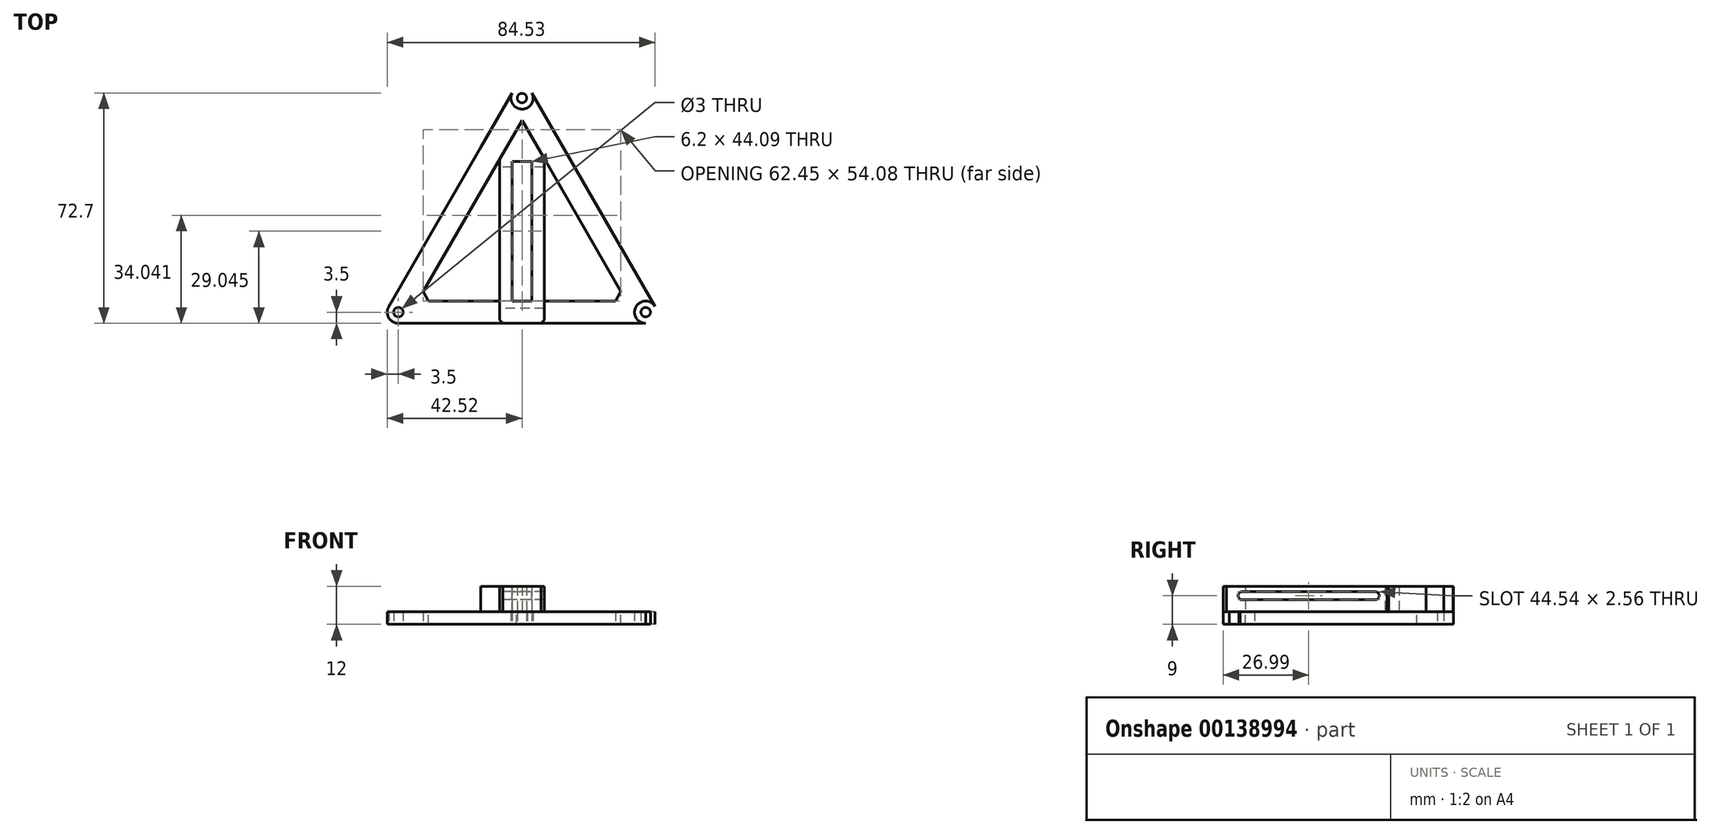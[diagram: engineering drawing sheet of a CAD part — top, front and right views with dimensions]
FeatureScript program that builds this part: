
annotation { "Feature Type Name" : "Feature", "Feature Type Description" : "" }
export const myFeature = defineFeature(function(context is Context, id is Id, definition is map)
    precondition{}
    {
        {
            var Q0;
            Q0=qCreatedBy(makeId("Top.planeOp"),FACE);
            var sketch = newSketch(context, id + "F0", { "sketchPlane" : qUnion([Q0])});
            skLineSegment(sketch, "E0", {"start": v(-21.7, -12.53) * mm, "end": v(0, 0) * mm});
            skLineSegment(sketch, "E1", {"start": v(-21.7, -12.53) * mm, "end": v(-39.02, -22.53) * mm, "construction": true});
            skCircle(sketch, "E2", {"center": v(-39.02, -22.53) * mm, "radius": 1.5 * mm});
            skLineSegment(sketch, "E3", {"start": v(-21.7, -12.53) * mm, "end": v(21.7, -12.53) * mm, "construction": true});
            skLineSegment(sketch, "E4", {"start": v(0, 25.06) * mm, "end": v(-21.7, -12.53) * mm, "construction": true});
            skLineSegment(sketch, "E5", {"start": v(0, 25.06) * mm, "end": v(21.7, -12.53) * mm, "construction": true});
            skLineSegment(sketch, "E6", {"start": v(0, 25.06) * mm, "end": v(0, -22.8) * mm, "construction": true});
            skPoint(sketch, "E6.endSnap0", {"position": v(0, -12.53) * mm});
            skLineSegment(sketch, "E7", {"start": v(0, 0) * mm, "end": v(-22.62, 13.06) * mm, "construction": true});
            skLineSegment(sketch, "E8", {"start": v(-21.7, -12.53) * mm, "end": v(23.8, 13.74) * mm, "construction": true});
            skLineSegment(sketch, "E9.MirrorCS", {"start": v(21.7, -12.53) * mm, "end": v(0, 0) * mm});
            skLineSegment(sketch, "E10.MirrorCS", {"start": v(21.7, -12.53) * mm, "end": v(-23.8, 13.74) * mm, "construction": true});
            skLineSegment(sketch, "E11.MirrorCS", {"start": v(21.7, -12.53) * mm, "end": v(-21.7, -12.53) * mm, "construction": true});
            skCircle(sketch, "E12.0", {"center": v(-39.02, -22.53) * mm, "radius": 3.5 * mm});
            skCircle(sketch, "E13.MirrorC", {"center": v(39.02, -22.53) * mm, "radius": 1.5 * mm});
            skCircle(sketch, "E14.MirrorC", {"center": v(39.02, -22.53) * mm, "radius": 3.5 * mm});
            skCircle(sketch, "E15.MirrorC", {"center": v(0, 45.06) * mm, "radius": 1.5 * mm});
            skCircle(sketch, "E16.MirrorC", {"center": v(0, 45.06) * mm, "radius": 3.5 * mm});
            skSolve(sketch);
        }
        {
            var Q0;
            Q0=makeQuery(id+"F0.imprint","IMPRINT",FACE,{"disambiguationData":[TD([[makeQuery(id+"F0.imprint","IMPRINT",EDGE,{"derivedFrom":sQuery(id+"F0.wireOp",EDGE,"E2")}),-1.0]])]});
            var Q1;
            Q1=makeQuery(id+"F0.imprint","IMPRINT",FACE,{"disambiguationData":[TD([[makeQuery(id+"F0.imprint","IMPRINT",EDGE,{"derivedFrom":sQuery(id+"F0.wireOp",EDGE,"E15.MirrorC")}),1.0]])]});
            var Q2;
            Q2=makeQuery(id+"F0.imprint","IMPRINT",FACE,{"disambiguationData":[TD([[makeQuery(id+"F0.imprint","IMPRINT",EDGE,{"derivedFrom":sQuery(id+"F0.wireOp",EDGE,"E13.MirrorC")}),1.0]])]});
            extrude(context, id + "F1", {"entities" : qUnion([Q0, Q1, Q2]), "depth" : 1 * mm});
        }
        {
            var Q0;
            Q0=makeQuery(id+"F1.opExtrude","CAP_FACE",FACE,{"disambiguationData":[OSD([sQuery(id+"F0.wireOp",EDGE,"E15.MirrorC"),sQuery(id+"F0.wireOp",EDGE,"E16.MirrorC")])],"isStart":false});
            var sketch = newSketch(context, id + "F2", { "sketchPlane" : qUnion([Q0])});
            skCircle(sketch, "E17.0", {"center": v(-39.02, -22.53) * mm, "radius": 3.5 * mm});
            skCircle(sketch, "E17.1", {"center": v(0, 45.06) * mm, "radius": 3.5 * mm});
            skCircle(sketch, "E17.2", {"center": v(39.02, -22.53) * mm, "radius": 3.5 * mm});
            skSolve(sketch);
        }
        {
            var Q0;
            Q0=qSketchRegion(id+"F2",true);
            extrude(context, id + "F3", {"entities" : qUnion([Q0]), "depth" : 1 * mm});
        }
        {
            var Q0;
            Q0=makeQuery(id+"F3.opExtrude","CAP_FACE",FACE,{"disambiguationData":[OSD([sQuery(id+"F2.wireOp",EDGE,"E17.0")])],"isStart":false});
            var sketch = newSketch(context, id + "F4", { "sketchPlane" : qUnion([Q0])});
            skCircle(sketch, "E18.0", {"center": v(0, 45.06) * mm, "radius": 3.5 * mm});
            skCircle(sketch, "E18.1", {"center": v(-39.02, -22.53) * mm, "radius": 3.5 * mm});
            skCircle(sketch, "E18.2", {"center": v(39.02, -22.53) * mm, "radius": 3.5 * mm});
            skLineSegment(sketch, "E19", {"start": v(-3.05, 46.77) * mm, "end": v(-42.05, -20.78) * mm});
            skLineSegment(sketch, "E20", {"start": v(3.03, 43.3) * mm, "end": v(-35.99, -24.28) * mm});
            skLineSegment(sketch, "E21", {"start": v(-3.03, 43.3) * mm, "end": v(35.99, -24.28) * mm});
            skLineSegment(sketch, "E22", {"start": v(3.03, 46.8) * mm, "end": v(42.05, -20.78) * mm});
            skLineSegment(sketch, "E23", {"start": v(39.02, -26.03) * mm, "end": v(-39.02, -26.03) * mm});
            skLineSegment(sketch, "E24", {"start": v(39.02, -19.03) * mm, "end": v(-39.02, -19.03) * mm});
            skSolve(sketch);
        }
        {
            var Q0;
            {var subQ0=sQuery(id+"F4.wireOp",EDGE,"E18.1");var subQ1=makeQuery(id+"F4.imprint","INTERSECT",VERTEX,{"derivedFrom":[subQ0,sQuery(id+"F4.wireOp",EDGE,"E19")]});Q0=makeQuery(id+"F4.imprint","IMPRINT",FACE,{"disambiguationData":[TD([[makeQuery(id+"F4.imprint","IMPRINT",EDGE,{"disambiguationData":[TD([[subQ1,1.0]])],"derivedFrom":subQ0}),1.0]])]});}
            var Q1;
            {var subQ0=sQuery(id+"F4.wireOp",EDGE,"E20");var subQ1=sQuery(id+"F4.wireOp",EDGE,"E18.1");var subQ2=makeQuery(id+"F4.imprint","INTERSECT",VERTEX,{"derivedFrom":[subQ1,subQ0]});Q1=makeQuery(id+"F4.imprint","IMPRINT",FACE,{"disambiguationData":[TD([[makeQuery(id+"F4.imprint","IMPRINT",EDGE,{"disambiguationData":[TD([[subQ2,-1.0]])],"derivedFrom":subQ1}),-1.0]])]});}
            var Q2;
            {var subQ7=sQuery(id+"F4.wireOp",EDGE,"E19");Q2=makeQuery(id+"F4.imprint","IMPRINT",FACE,{"disambiguationData":[TD([[makeQuery(id+"F4.imprint","IMPRINT",EDGE,{"derivedFrom":subQ7}),1.0]])]});}
            var Q3;
            {var subQ9=sQuery(id+"F4.wireOp",EDGE,"E23");Q3=makeQuery(id+"F4.imprint","IMPRINT",FACE,{"disambiguationData":[TD([[makeQuery(id+"F4.imprint","IMPRINT",EDGE,{"derivedFrom":subQ9}),-1.0]])]});}
            var Q4;
            {var subQ9=sQuery(id+"F4.wireOp",EDGE,"E22");Q4=makeQuery(id+"F4.imprint","IMPRINT",FACE,{"disambiguationData":[TD([[makeQuery(id+"F4.imprint","IMPRINT",EDGE,{"derivedFrom":subQ9}),-1.0]])]});}
            var Q5;
            {var subQ0=sQuery(id+"F4.wireOp",EDGE,"E21");var subQ1=sQuery(id+"F4.wireOp",EDGE,"E18.2");var subQ2=makeQuery(id+"F4.imprint","INTERSECT",VERTEX,{"derivedFrom":[subQ1,subQ0]});Q5=makeQuery(id+"F4.imprint","IMPRINT",FACE,{"disambiguationData":[TD([[makeQuery(id+"F4.imprint","IMPRINT",EDGE,{"disambiguationData":[TD([[subQ2,-1.0]])],"derivedFrom":subQ1}),1.0]])]});}
            var Q6;
            {var subQ0=sQuery(id+"F4.wireOp",EDGE,"E20");var subQ1=sQuery(id+"F4.wireOp",EDGE,"E18.0");var subQ2=makeQuery(id+"F4.imprint","INTERSECT",VERTEX,{"derivedFrom":[subQ1,subQ0]});Q6=makeQuery(id+"F4.imprint","IMPRINT",FACE,{"disambiguationData":[TD([[makeQuery(id+"F4.imprint","IMPRINT",EDGE,{"disambiguationData":[TD([[subQ2,-1.0]])],"derivedFrom":subQ1}),1.0]])]});}
            var Q7;
            {var subQ0=sQuery(id+"F4.wireOp",EDGE,"E18.2");var subQ1=makeQuery(id+"F4.imprint","INTERSECT",VERTEX,{"derivedFrom":[subQ0,sQuery(id+"F4.wireOp",EDGE,"E21")]});Q7=makeQuery(id+"F4.imprint","IMPRINT",FACE,{"disambiguationData":[TD([[makeQuery(id+"F4.imprint","IMPRINT",EDGE,{"disambiguationData":[TD([[subQ1,1.0]])],"derivedFrom":subQ0}),-1.0]])]});}
            var Q8;
            {var subQ0=sQuery(id+"F4.wireOp",EDGE,"E18.0");var subQ1=makeQuery(id+"F4.imprint","INTERSECT",VERTEX,{"derivedFrom":[subQ0,sQuery(id+"F4.wireOp",EDGE,"E20")]});Q8=makeQuery(id+"F4.imprint","IMPRINT",FACE,{"disambiguationData":[TD([[makeQuery(id+"F4.imprint","IMPRINT",EDGE,{"disambiguationData":[TD([[subQ1,-1.0]])],"derivedFrom":subQ0}),-1.0]])]});}
            extrude(context, id + "F5", {"entities" : qUnion([Q0, Q1, Q2, Q3, Q4, Q5, Q6, Q7, Q8]), "depth" : 4 * mm});
        }
        {
            var Q0;
            Q0=makeQuery(id+"F5.opExtrude","CAP_FACE",FACE,{"disambiguationData":[OSD([sQuery(id+"F4.wireOp",EDGE,"E18.0"),sQuery(id+"F4.wireOp",EDGE,"E18.1"),sQuery(id+"F4.wireOp",EDGE,"E18.2"),sQuery(id+"F4.wireOp",EDGE,"E19"),sQuery(id+"F4.wireOp",EDGE,"E20"),sQuery(id+"F4.wireOp",EDGE,"E21"),sQuery(id+"F4.wireOp",EDGE,"E22"),sQuery(id+"F4.wireOp",EDGE,"E23"),sQuery(id+"F4.wireOp",EDGE,"E24")])],"isStart":false});
            var sketch = newSketch(context, id + "F6", { "sketchPlane" : qUnion([Q0])});
            skCircle(sketch, "E25.0", {"center": v(39.02, -22.53) * mm, "radius": 3.5 * mm});
            skCircle(sketch, "E26.0", {"center": v(-39.02, -22.53) * mm, "radius": 3.5 * mm});
            skCircle(sketch, "E27.0", {"center": v(0, 45.06) * mm, "radius": 3.5 * mm});
            skLineSegment(sketch, "E28.bottom", {"start": v(-3.1, 25.06) * mm, "end": v(3.1, 25.06) * mm});
            skLineSegment(sketch, "E28.top", {"start": v(-3.1, -26.03) * mm, "end": v(3.1, -26.03) * mm});
            skLineSegment(sketch, "E28.left", {"start": v(-3.1, 25.06) * mm, "end": v(-3.1, -26.03) * mm});
            skLineSegment(sketch, "E28.right", {"start": v(3.1, 25.06) * mm, "end": v(3.1, -26.03) * mm});
            skArc(sketch, "E29", {"start": v(3.03, 46.8) * mm, "mid": v(-0.02, 48.53) * mm, "end": v(-3.05, 46.77) * mm});
            skLineSegment(sketch, "E30", {"start": v(-3.05, 46.77) * mm, "end": v(-13.05, 29.45) * mm, "construction": true});
            skLineSegment(sketch, "E31", {"start": v(3.03, 46.8) * mm, "end": v(13.03, 29.49) * mm, "construction": true});
            skLineSegment(sketch, "E32", {"start": v(-13.05, 29.45) * mm, "end": v(-7, 25.95) * mm, "construction": true});
            skLineSegment(sketch, "E33", {"start": v(7, 25.95) * mm, "end": v(13.03, 29.49) * mm, "construction": true});
            skLineSegment(sketch, "E34", {"start": v(-3.05, 46.77) * mm, "end": v(-13.05, 29.45) * mm});
            skLineSegment(sketch, "E35", {"start": v(-7, 25.95) * mm, "end": v(-13.05, 29.45) * mm});
            skLineSegment(sketch, "E36", {"start": v(3.03, 46.8) * mm, "end": v(13.03, 29.49) * mm});
            skLineSegment(sketch, "E37", {"start": v(13.03, 29.49) * mm, "end": v(7, 25.95) * mm});
            skLineSegment(sketch, "E38", {"start": v(-7, 25.95) * mm, "end": v(-7, -26.03) * mm});
            skLineSegment(sketch, "E39", {"start": v(-7, -26.03) * mm, "end": v(-3.1, -26.03) * mm});
            skLineSegment(sketch, "E40", {"start": v(7, 25.95) * mm, "end": v(7, -26.03) * mm});
            skLineSegment(sketch, "E41", {"start": v(7, -26.03) * mm, "end": v(3.1, -26.03) * mm});
            skSolve(sketch);
        }
        {
            var Q0;
            {var subQ0=sQuery(id+"F6.wireOp",EDGE,"E29");Q0=makeQuery(id+"F6.imprint","IMPRINT",FACE,{"disambiguationData":[TD([[makeQuery(id+"F6.imprint","IMPRINT",EDGE,{"derivedFrom":subQ0}),-1.0]])]});}
            var Q1;
            {var subQ0=sQuery(id+"F6.wireOp",EDGE,"E29");Q1=makeQuery(id+"F6.imprint","IMPRINT",FACE,{"disambiguationData":[TD([[makeQuery(id+"F6.imprint","IMPRINT",EDGE,{"derivedFrom":subQ0}),1.0]])]});}
            var Q2;
            {var subQ2=sQuery(id+"F6.wireOp",EDGE,"E34");Q2=makeQuery(id+"F6.imprint","IMPRINT",FACE,{"disambiguationData":[TD([[makeQuery(id+"F6.imprint","IMPRINT",EDGE,{"derivedFrom":subQ2}),1.0]])]});}
            var Q3;
            Q3=makeQuery(id+"F6.imprint","IMPRINT",FACE,{"disambiguationData":[TD([[makeQuery(id+"F6.imprint","IMPRINT",EDGE,{"derivedFrom":sQuery(id+"F6.wireOp",EDGE,"E28.bottom")}),1.0]])]});
            var Q4;
            {var subQ0=sQuery(id+"F6.wireOp",EDGE,"E39");Q4=makeQuery(id+"F6.imprint","IMPRINT",FACE,{"disambiguationData":[TD([[makeQuery(id+"F6.imprint","IMPRINT",EDGE,{"derivedFrom":subQ0}),-1.0]])]});}
            var Q5;
            {var subQ0=sQuery(id+"F6.wireOp",EDGE,"E41");Q5=makeQuery(id+"F6.imprint","IMPRINT",FACE,{"disambiguationData":[TD([[makeQuery(id+"F6.imprint","IMPRINT",EDGE,{"derivedFrom":subQ0}),-1.0]])]});}
            var Q6;
            {var subQ0=sQuery(id+"F6.wireOp",EDGE,"E28.top");Q6=makeQuery(id+"F6.imprint","IMPRINT",FACE,{"disambiguationData":[TD([[makeQuery(id+"F6.imprint","IMPRINT",EDGE,{"derivedFrom":subQ0}),-1.0]])]});}
            extrude(context, id + "F7", {"entities" : qUnion([Q0, Q1, Q2, Q3, Q4, Q5, Q6]), "depth" : 8 * mm});
        }
        {
            var Q0;
            Q0=makeQuery(id+"F7.opExtrude","SWEPT_FACE",FACE,{"disambiguationData":[OSD([sQuery(id+"F6.wireOp",EDGE,"E38")])]});
            var sketch = newSketch(context, id + "F8", { "sketchPlane" : qUnion([Q0])});
            skLineSegment(sketch, "E42", {"start": v(-25.95, 8.8) * mm, "end": v(26.03, 8.8) * mm, "construction": true});
            skCircle(sketch, "E43", {"center": v(-21.95, 11) * mm, "radius": 1.28 * mm});
            skCircle(sketch, "E44", {"center": v(20.03, 11) * mm, "radius": 1.28 * mm});
            skLineSegment(sketch, "E45", {"start": v(-21.95, 12.28) * mm, "end": v(20.03, 12.28) * mm});
            skLineSegment(sketch, "E46", {"start": v(20.03, 9.72) * mm, "end": v(-21.95, 9.72) * mm});
            skSolve(sketch);
        }
        {
            var Q0;
            Q0=qSketchRegion(id+"F8",true);
            extrude(context, id + "F9", {"entities" : qUnion([Q0]), "operationType" : NewBodyOperationType.REMOVE, "oppositeDirection" : true, "depth" : 25 * mm});
        }
        {
            var Q0;
            Q0=makeQuery(id+"F7.opExtrude","SWEPT_EDGE",EDGE,{"disambiguationData":[OSD([sQuery(id+"F4.wireOp",EDGE,"E20"),sQuery(id+"F6.wireOp",EDGE,"E35"),sQuery(id+"F6.wireOp",EDGE,"E38")])]});
            var Q1;
            Q1=makeQuery(id+"F7.opExtrude","SWEPT_EDGE",EDGE,{"disambiguationData":[OSD([sQuery(id+"F4.wireOp",EDGE,"E21"),sQuery(id+"F6.wireOp",EDGE,"E37"),sQuery(id+"F6.wireOp",EDGE,"E40")])]});
            var Q2;
            Q2=makeQuery(id+"F7.opExtrude","SWEPT_EDGE",EDGE,{"disambiguationData":[OSD([sQuery(id+"F6.wireOp",EDGE,"E38"),sQuery(id+"F6.wireOp",EDGE,"E39")])]});
            var Q3;
            Q3=makeQuery(id+"F7.opExtrude","SWEPT_EDGE",EDGE,{"disambiguationData":[OSD([sQuery(id+"F6.wireOp",EDGE,"E40"),sQuery(id+"F6.wireOp",EDGE,"E41")])]});
            chamfer(context, id + "F10", {"entities" : qUnion([Q0, Q1, Q2, Q3]), "width" : 1 * mm, "tangentPropagation" : true});
        }
        {
            var Q0;
            Q0=makeQuery(id+"F5.opExtrude","SWEPT_EDGE",EDGE,{"disambiguationData":[OSD([sQuery(id+"F4.wireOp",EDGE,"E20"),sQuery(id+"F4.wireOp",EDGE,"E24")])]});
            var Q1;
            Q1=makeQuery(id+"F5.opExtrude","SWEPT_EDGE",EDGE,{"disambiguationData":[OSD([sQuery(id+"F4.wireOp",EDGE,"E21"),sQuery(id+"F4.wireOp",EDGE,"E24")])]});
            var Q2;
            Q2=makeQuery(id+"F5.opExtrude","SWEPT_EDGE",EDGE,{"disambiguationData":[OSD([sQuery(id+"F4.wireOp",EDGE,"E20"),sQuery(id+"F4.wireOp",EDGE,"E21")])]});
            var Q3;
            Q3=makeQuery(id+"F7.opExtrude","SWEPT_EDGE",EDGE,{"disambiguationData":[OSD([sQuery(id+"F4.wireOp",EDGE,"E19"),sQuery(id+"F6.wireOp",EDGE,"E34"),sQuery(id+"F6.wireOp",EDGE,"E35")])]});
            var Q4;
            Q4=makeQuery(id+"F7.opExtrude","SWEPT_EDGE",EDGE,{"disambiguationData":[OSD([sQuery(id+"F4.wireOp",EDGE,"E22"),sQuery(id+"F6.wireOp",EDGE,"E36"),sQuery(id+"F6.wireOp",EDGE,"E37")])]});
            chamfer(context, id + "F11", {"entities" : qUnion([Q0, Q1, Q2, Q3, Q4]), "width" : 2 * mm, "tangentPropagation" : true});
        }
        {
            var Q0;
            Q0=makeQuery(id+"F0.imprint","IMPRINT",FACE,{"disambiguationData":[TD([[makeQuery(id+"F0.imprint","IMPRINT",EDGE,{"derivedFrom":sQuery(id+"F0.wireOp",EDGE,"E2")}),1.0]])]});
            var Q1;
            Q1=makeQuery(id+"F0.imprint","IMPRINT",FACE,{"disambiguationData":[TD([[makeQuery(id+"F0.imprint","IMPRINT",EDGE,{"derivedFrom":sQuery(id+"F0.wireOp",EDGE,"E15.MirrorC")}),-1.0]])]});
            var Q2;
            Q2=makeQuery(id+"F0.imprint","IMPRINT",FACE,{"disambiguationData":[TD([[makeQuery(id+"F0.imprint","IMPRINT",EDGE,{"derivedFrom":sQuery(id+"F0.wireOp",EDGE,"E13.MirrorC")}),-1.0]])]});
            extrude(context, id + "F12", {"entities" : qUnion([Q0, Q1, Q2]), "operationType" : NewBodyOperationType.REMOVE, "depth" : 25 * mm});
        }
        {
            var Q0;
            Q0=makeQuery(id+"F1.opExtrude","SWEPT_BODY",BODY,{"disambiguationData":[OSD([sQuery(id+"F0.wireOp",EDGE,"E15.MirrorC"),sQuery(id+"F0.wireOp",EDGE,"E16.MirrorC")])]});
            var Q1;
            Q1=makeQuery(id+"F1.opExtrude","SWEPT_BODY",BODY,{"disambiguationData":[OSD([sQuery(id+"F0.wireOp",EDGE,"E13.MirrorC"),sQuery(id+"F0.wireOp",EDGE,"E14.MirrorC")])]});
            var Q2;
            Q2=makeQuery(id+"F1.opExtrude","SWEPT_BODY",BODY,{"disambiguationData":[OSD([sQuery(id+"F0.wireOp",EDGE,"E2"),sQuery(id+"F0.wireOp",EDGE,"E12.0")])]});
            var Q3;
            Q3=makeQuery(id+"F3.opExtrude","SWEPT_BODY",BODY,{"disambiguationData":[OSD([sQuery(id+"F2.wireOp",EDGE,"E17.0")])]});
            var Q4;
            Q4=makeQuery(id+"F3.opExtrude","SWEPT_BODY",BODY,{"disambiguationData":[OSD([sQuery(id+"F2.wireOp",EDGE,"E17.2")])]});
            var Q5;
            Q5=makeQuery(id+"F3.opExtrude","SWEPT_BODY",BODY,{"disambiguationData":[OSD([sQuery(id+"F2.wireOp",EDGE,"E17.1")])]});
            deleteBodies(context, id + "F13", {"entities" : qUnion([Q0, Q1, Q2, Q3, Q4, Q5])});
        }
    });
